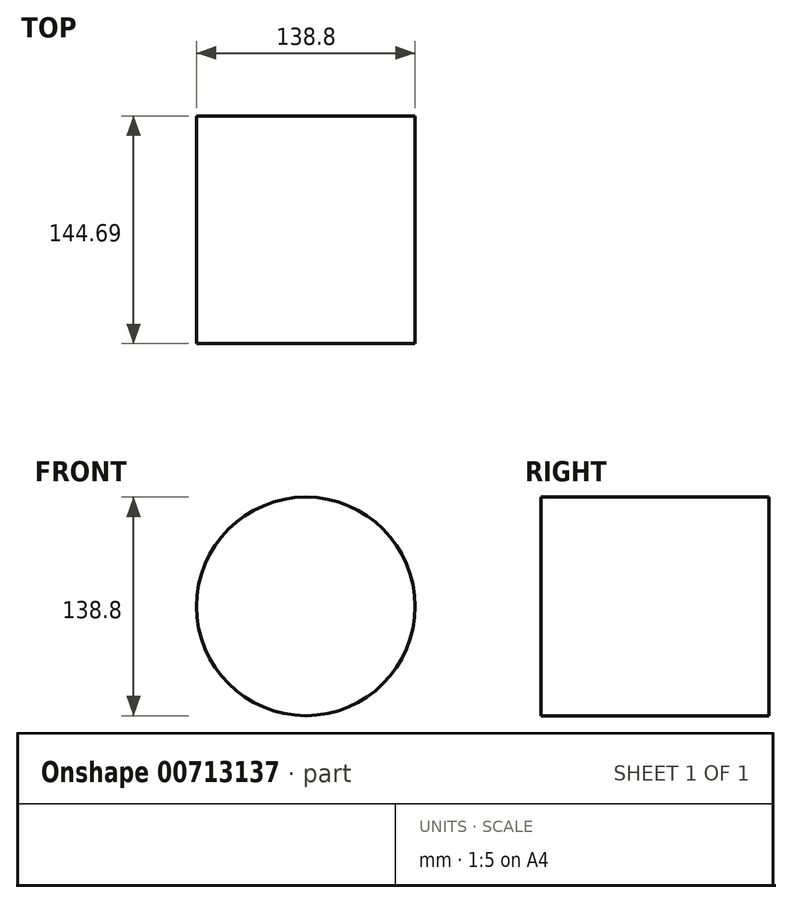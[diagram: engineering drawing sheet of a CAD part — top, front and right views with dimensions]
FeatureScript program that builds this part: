
annotation { "Feature Type Name" : "Feature", "Feature Type Description" : "" }
export const myFeature = defineFeature(function(context is Context, id is Id, definition is map)
    precondition{}
    {
        {
            var Q0;
            Q0=qCreatedBy(makeId("Front.planeOp"),FACE);
            var sketch = newSketch(context, id + "F0", { "sketchPlane" : qUnion([Q0])});
            skCircle(sketch, "E0", {"center": v(0, 0) * mm, "radius": 69.4 * mm});
            skSolve(sketch);
        }
        {
            var Q0;
            Q0=makeQuery(id+"F0.imprint","IMPRINT",FACE,{"disambiguationData":[TD([[makeQuery(id+"F0.imprint","IMPRINT",EDGE,{"derivedFrom":sQuery(id+"F0.wireOp",EDGE,"E0")}),1.0]])]});
            extrude(context, id + "F1", {"entities" : qUnion([Q0]), "depth" : 144.7 * mm, "offsetDistance" : 25.4 * mm});
        }
    });
